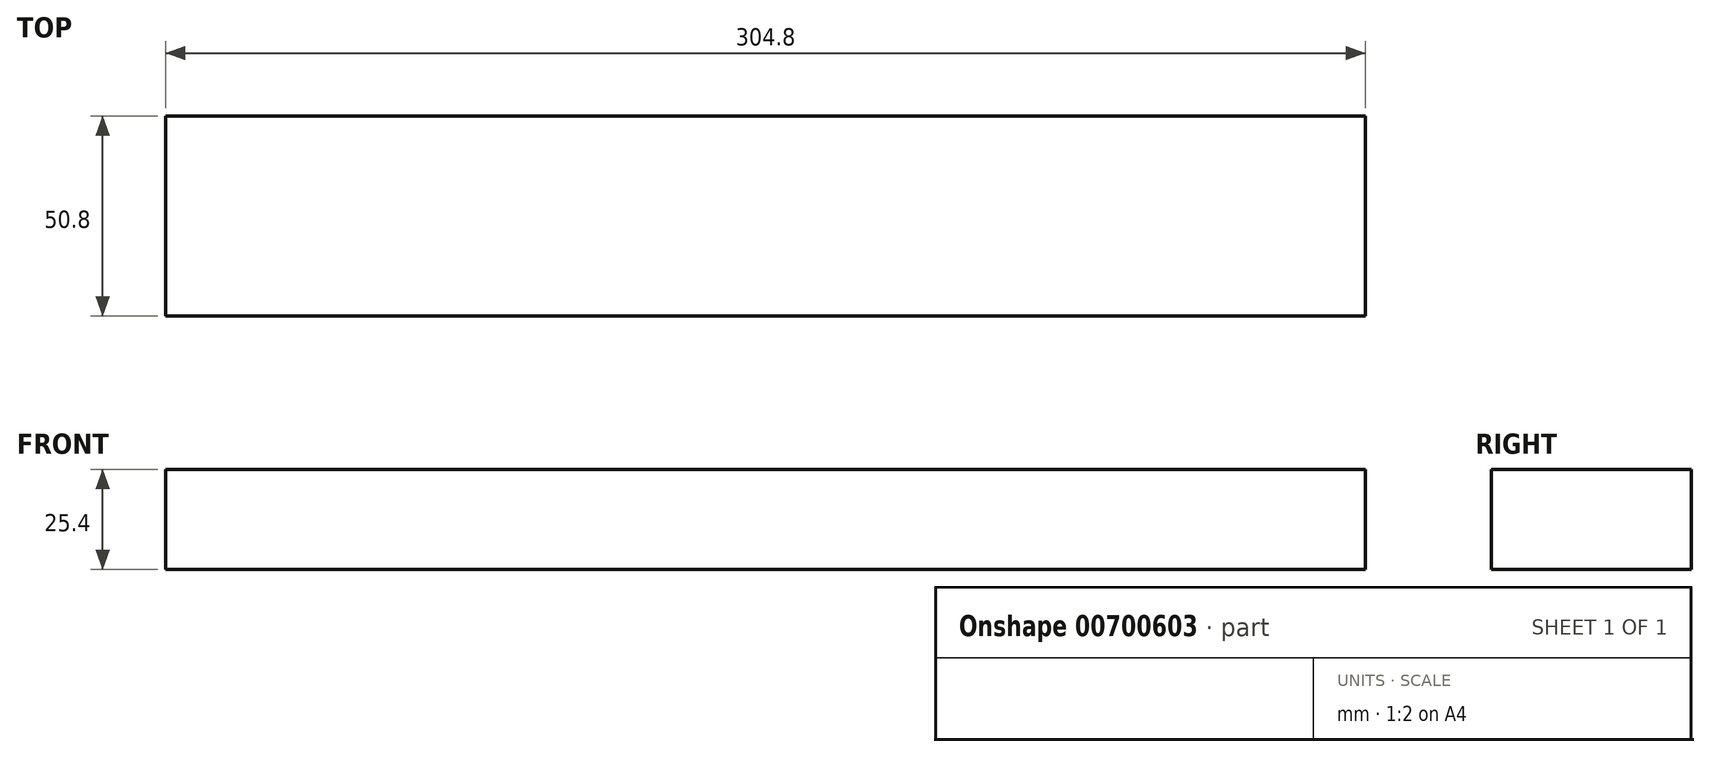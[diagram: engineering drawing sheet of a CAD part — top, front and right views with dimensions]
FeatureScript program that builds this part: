
annotation { "Feature Type Name" : "Feature", "Feature Type Description" : "" }
export const myFeature = defineFeature(function(context is Context, id is Id, definition is map)
    precondition{}
    {
        {
            var Q0;
            Q0=qCreatedBy(makeId("Top.planeOp"),FACE);
            var sketch = newSketch(context, id + "F0", { "sketchPlane" : qUnion([Q0])});
            skLineSegment(sketch, "E0.bottom", {"start": v(-152.4, -25.4) * mm, "end": v(152.4, -25.4) * mm});
            skLineSegment(sketch, "E0.top", {"start": v(-152.4, 25.4) * mm, "end": v(152.4, 25.4) * mm});
            skLineSegment(sketch, "E0.left", {"start": v(-152.4, -25.4) * mm, "end": v(-152.4, 25.4) * mm});
            skLineSegment(sketch, "E0.right", {"start": v(152.4, -25.4) * mm, "end": v(152.4, 25.4) * mm});
            skPoint(sketch, "E0.middle", {"position": v(0, 0) * mm});
            skSolve(sketch);
        }
        {
            var Q0;
            Q0 = qSketchRegion(id + "F0", true);
            extrude(context, id + "F1", {"entities" : qUnion([Q0]), "depth" : 25.4 * mm, "offsetDistance" : 25.4 * mm});
        }
    });
